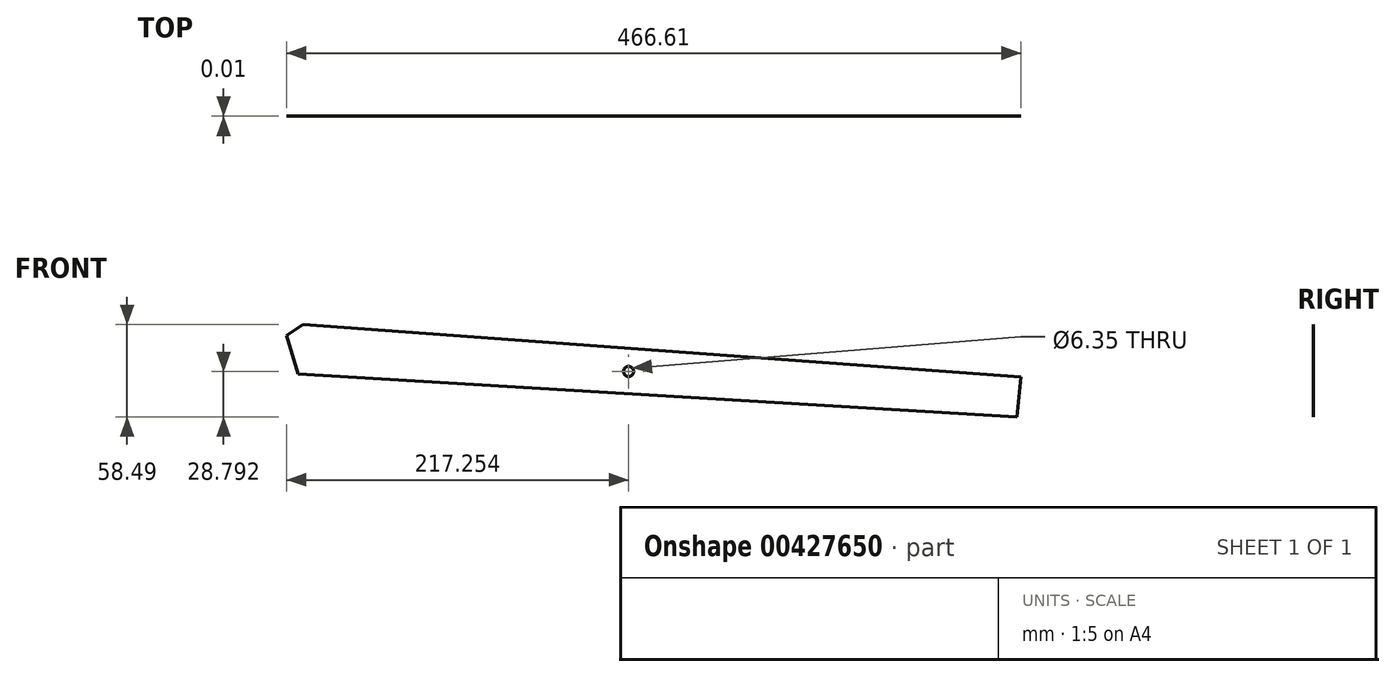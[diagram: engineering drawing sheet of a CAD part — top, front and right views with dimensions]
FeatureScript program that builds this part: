
annotation { "Feature Type Name" : "Feature", "Feature Type Description" : "" }
export const myFeature = defineFeature(function(context is Context, id is Id, definition is map)
    precondition{}
    {
        {
            var Q0;
            Q0=qCreatedBy(makeId("Front.planeOp"),FACE);
            var sketch = newSketch(context, id + "F0", { "sketchPlane" : qUnion([Q0])});
            skLineSegment(sketch, "E0", {"start": v(-253.12, 73.68) * mm, "end": v(-245.72, 49.39) * mm});
            skLineSegment(sketch, "E1", {"start": v(-245.72, 49.39) * mm, "end": v(210.67, 22.15) * mm});
            skLineSegment(sketch, "E2", {"start": v(210.67, 22.15) * mm, "end": v(213.5, 47.4) * mm});
            skLineSegment(sketch, "E3", {"start": v(213.5, 47.4) * mm, "end": v(-242.5, 80.64) * mm});
            skLineSegment(sketch, "E4", {"start": v(-242.5, 80.64) * mm, "end": v(-253.12, 73.68) * mm});
            skSolve(sketch);
        }
        {
            var Q0;
            Q0=makeQuery(id+"F0.imprint","IMPRINT",FACE,{"disambiguationData":[TD([[makeQuery(id+"F0.imprint","IMPRINT",EDGE,{"derivedFrom":sQuery(id+"F0.wireOp",EDGE,"E0")}),1.0]])]});
            var Q1;
            Q1 = qSketchRegion(id + "F0", true);
            extrude(context, id + "F1", {"entities" : qUnion([Q0, Q1]), "depth" : 1 / 101.6 * mm});
        }
        {
            var Q0;
            Q0=makeQuery(id+"F1.opExtrude","CAP_FACE",FACE,{"disambiguationData":[OSD([sQuery(id+"F0.wireOp",EDGE,"E0"),sQuery(id+"F0.wireOp",EDGE,"E1"),sQuery(id+"F0.wireOp",EDGE,"E2"),sQuery(id+"F0.wireOp",EDGE,"E3"),sQuery(id+"F0.wireOp",EDGE,"E4")])],"isStart":false});
            var sketch = newSketch(context, id + "F2", { "sketchPlane" : qUnion([Q0])});
            skCircle(sketch, "E5", {"center": v(-35.87, 50.94) * mm, "radius": 1.59 * mm});
            skSolve(sketch);
        }
        {
            var Q0;
            Q0=sQuery(id+"F2.wireOp",VERTEX,"E5.center");
            var Q1;
            Q1=makeQuery(id+"F1.opExtrude","SWEPT_BODY",BODY,{"disambiguationData":[OSD([sQuery(id+"F0.wireOp",EDGE,"E0"),sQuery(id+"F0.wireOp",EDGE,"E1"),sQuery(id+"F0.wireOp",EDGE,"E2"),sQuery(id+"F0.wireOp",EDGE,"E3"),sQuery(id+"F0.wireOp",EDGE,"E4")])]});
            hole(context, id + "F3", {"style" : HoleStyle.SIMPLE, "endStyle" : HoleEndStyle.THROUGH, "holeDiameter" : 6.35 * mm, "isTappedThrough" : true, "tappedDepth" : 12.7 * mm, "tapClearance" : 3, "locations" : qUnion([Q0]), "scope" : qUnion([Q1])});
        }
    });
